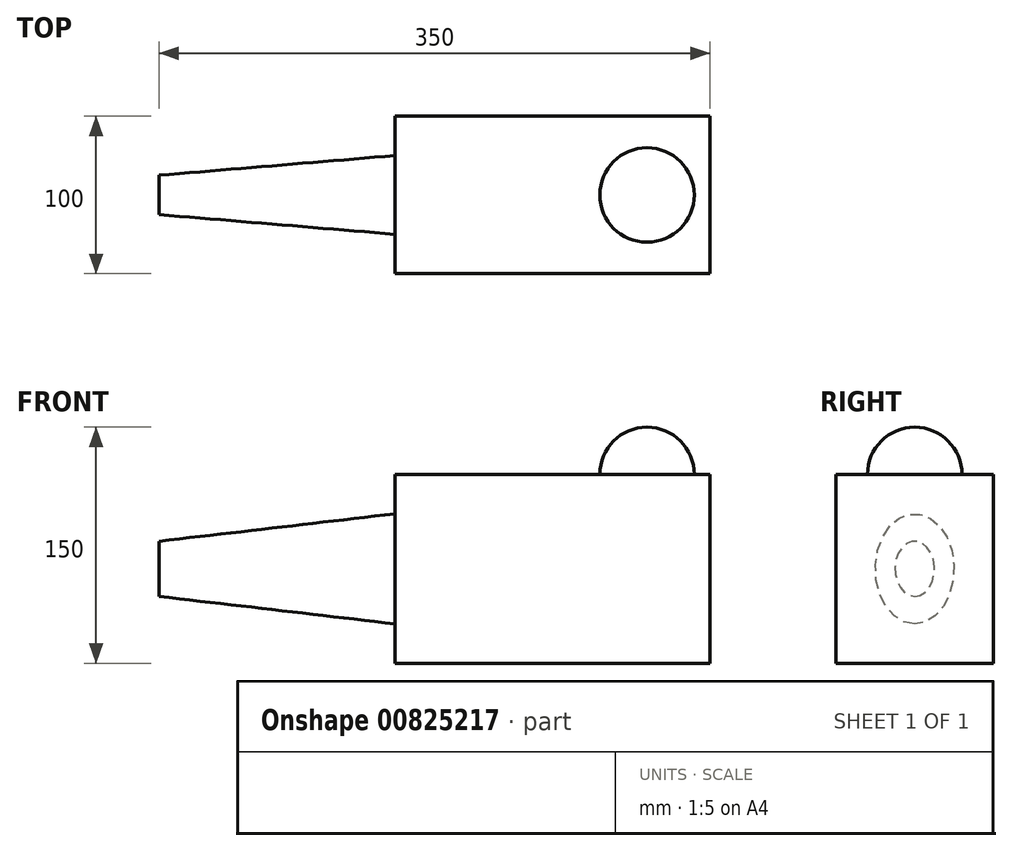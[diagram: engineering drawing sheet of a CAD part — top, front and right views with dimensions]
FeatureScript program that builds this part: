
annotation { "Feature Type Name" : "Feature", "Feature Type Description" : "" }
export const myFeature = defineFeature(function(context is Context, id is Id, definition is map)
    precondition{}
    {
        {
            var Q0;
            Q0=qCreatedBy(makeId("Top.planeOp"),FACE);
            var sketch = newSketch(context, id + "F0", { "sketchPlane" : qUnion([Q0])});
            skLineSegment(sketch, "E0.bottom", {"start": v(-100, -50) * mm, "end": v(100, -50) * mm});
            skLineSegment(sketch, "E0.top", {"start": v(-100, 50) * mm, "end": v(100, 50) * mm});
            skLineSegment(sketch, "E0.left", {"start": v(-100, -50) * mm, "end": v(-100, 50) * mm});
            skLineSegment(sketch, "E0.right", {"start": v(100, -50) * mm, "end": v(100, 50) * mm});
            skPoint(sketch, "E0.middle", {"position": v(0, 0) * mm});
            skSolve(sketch);
        }
        {
            var Q0;
            Q0 = qSketchRegion(id + "F0", true);
            extrude(context, id + "F1", {"entities" : qUnion([Q0]), "depth" : 120 * mm, "offsetDistance" : 25 * mm});
        }
        {
            var Q0;
            Q0=makeQuery(id+"F1.opExtrude","CAP_FACE",FACE,{"disambiguationData":[OSD([sQuery(id+"F0.wireOp",EDGE,"E0.bottom"),sQuery(id+"F0.wireOp",EDGE,"E0.top"),sQuery(id+"F0.wireOp",EDGE,"E0.left"),sQuery(id+"F0.wireOp",EDGE,"E0.right")])],"isStart":false});
            var sketch = newSketch(context, id + "F2", { "sketchPlane" : qUnion([Q0])});
            skArc(sketch, "E1", {"start": v(60, -30) * mm, "mid": v(90, 0) * mm, "end": v(60, 30) * mm});
            skLineSegment(sketch, "E2", {"start": v(60, 30) * mm, "end": v(60, -30) * mm});
            skLineSegment(sketch, "E3", {"start": v(-100, 0) * mm, "end": v(100, 0) * mm, "construction": true});
            skSolve(sketch);
        }
        {
            var Q0;
            Q0 = qSketchRegion(id + "F2", true);
            var Q1;
            Q1=sQuery(id+"F2.wireOp",EDGE,"E2");
            revolve(context, id + "F3", {"operationType" : NewBodyOperationType.ADD, "surfaceOperationType" : NewSurfaceOperationType.NEW, "entities" : qUnion([Q0]), "axis" : qUnion([Q1]), "revolveType" : RevolveType.FULL});
        }
        {
            var Q0;
            Q0=makeQuery(id+"F1.opExtrude","SWEPT_FACE",FACE,{"disambiguationData":[OSD([sQuery(id+"F0.wireOp",EDGE,"E0.left")])]});
            var sketch = newSketch(context, id + "F4", { "sketchPlane" : qUnion([Q0])});
            skEllipse(sketch, "E4", {"center": v(0, 60) * mm, "majorRadius": 35 * mm, "minorRadius": 25 * mm, "majorAxis": v(0, -1)});
            skPoint(sketch, "E4.centerSnap0", {"position": v(0, 120) * mm});
            skLineSegment(sketch, "E5", {"start": v(50, 60) * mm, "end": v(-50, 60) * mm, "construction": true});
            skSolve(sketch);
        }
        {
            var Q0;
            Q0=qCreatedBy(makeId("Right.planeOp"),FACE);
            cPlane(context, id + "F5", {"entities" : qUnion([Q0]), "cplaneType" : CPlaneType.OFFSET, "offset" : 250 * mm, "oppositeDirection" : true, "width" : 150 * mm, "height" : 150 * mm});
        }
        {
            var Q0;
            Q0=qCreatedBy(id+"F5.planeOp",FACE);
            var sketch = newSketch(context, id + "F6", { "sketchPlane" : qUnion([Q0])});
            skEllipse(sketch, "E6", {"center": v(0, 60) * mm, "majorRadius": 17.5 * mm, "minorRadius": 12.5 * mm, "majorAxis": v(0, -1)});
            skSolve(sketch);
        }
        {
            var Q1;
            Q1=makeQuery(id+"F4.imprint","IMPRINT",FACE,{"disambiguationData":[TD([[makeQuery(id+"F4.imprint","IMPRINT",EDGE,{"derivedFrom":sQuery(id+"F4.wireOp",EDGE,"E4")}),1.0]])]});
            var Q2;
            Q2=makeQuery(id+"F6.imprint","IMPRINT",FACE,{"disambiguationData":[TD([[makeQuery(id+"F6.imprint","IMPRINT",EDGE,{"derivedFrom":sQuery(id+"F6.wireOp",EDGE,"E6")}),1.0]])]});
            loft(context, id + "F7", {"operationType" : NewBodyOperationType.ADD, "sheetProfilesArray" : [{ "sheetProfileEntities" : qUnion([Q1]) }, { "sheetProfileEntities" : qUnion([Q2]) }]});
        }
    });
